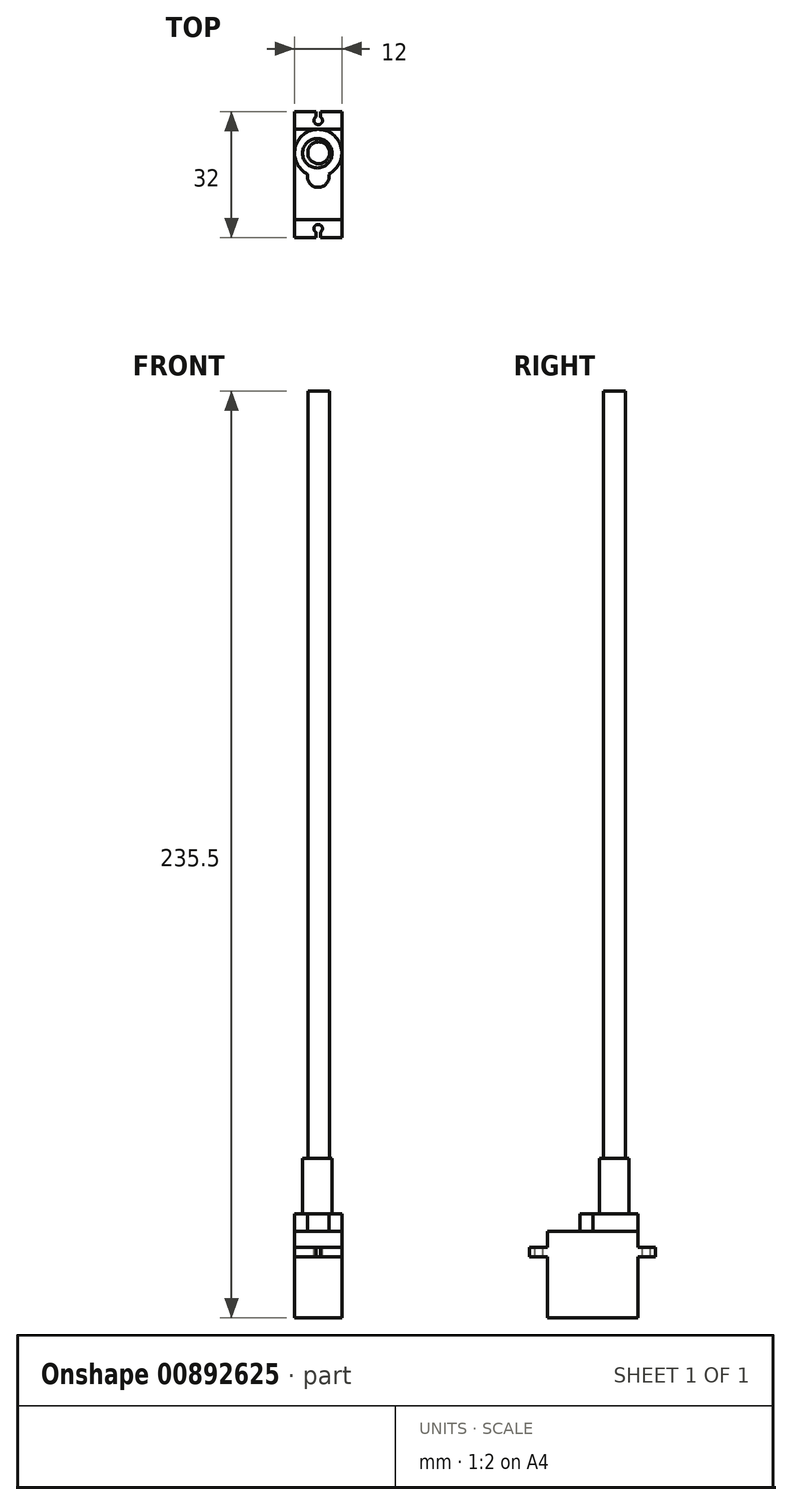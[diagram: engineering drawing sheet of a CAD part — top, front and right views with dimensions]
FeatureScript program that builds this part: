
annotation { "Feature Type Name" : "Feature", "Feature Type Description" : "" }
export const myFeature = defineFeature(function(context is Context, id is Id, definition is map)
    precondition{}
    {
        {
            var Q0;
            Q0=qCreatedBy(makeId("Top.planeOp"),FACE);
            var sketch = newSketch(context, id + "F0", { "sketchPlane" : qUnion([Q0])});
            skLineSegment(sketch, "E0.bottom", {"start": v(0, 0) * mm, "end": v(12, 0) * mm});
            skLineSegment(sketch, "E0.top", {"start": v(0, 23) * mm, "end": v(12, 23) * mm});
            skLineSegment(sketch, "E0.left", {"start": v(0, 0) * mm, "end": v(0, 23) * mm});
            skLineSegment(sketch, "E0.right", {"start": v(12, 0) * mm, "end": v(12, 23) * mm});
            skSolve(sketch);
        }
        {
            var Q0;
            Q0=qSketchRegion(id+"F0",true);
            extrude(context, id + "F1", {"entities" : qUnion([Q0]), "depth" : 22 * mm, "offsetDistance" : 25 * mm});
        }
        {
            var Q0;
            Q0=qCreatedBy(makeId("Top.planeOp"),FACE);
            cPlane(context, id + "F2", {"entities" : qUnion([Q0]), "cplaneType" : CPlaneType.OFFSET, "offset" : 15.5 * mm, "width" : 150 * mm, "height" : 150 * mm});
        }
        {
            var Q0;
            Q0=qCreatedBy(id+"F2.planeOp",FACE);
            var sketch = newSketch(context, id + "F3", { "sketchPlane" : qUnion([Q0])});
            skLineSegment(sketch, "E1.0", {"start": v(0, 23) * mm, "end": v(12, 23) * mm});
            skPoint(sketch, "E2.0", {"position": v(0, 11.5) * mm});
            skPoint(sketch, "E3.0", {"position": v(12, 11.5) * mm});
            skLineSegment(sketch, "E4", {"start": v(0, 11.5) * mm, "end": v(12, 11.5) * mm, "construction": true});
            skLineSegment(sketch, "E5", {"start": v(0, 23) * mm, "end": v(0, 27.5) * mm});
            skLineSegment(sketch, "E6", {"start": v(0, 27.5) * mm, "end": v(12, 27.5) * mm});
            skLineSegment(sketch, "E7", {"start": v(12, 27.5) * mm, "end": v(12, 23) * mm});
            skLineSegment(sketch, "E8.MirrorCS", {"start": v(0, 0) * mm, "end": v(12, 0) * mm});
            skLineSegment(sketch, "E9.MirrorCS", {"start": v(0, 0) * mm, "end": v(0, -4.5) * mm});
            skLineSegment(sketch, "E10.MirrorCS", {"start": v(0, -4.5) * mm, "end": v(12, -4.5) * mm});
            skLineSegment(sketch, "E11.MirrorCS", {"start": v(12, -4.5) * mm, "end": v(12, 0) * mm});
            skSolve(sketch);
        }
        {
            var Q0;
            Q0=qSketchRegion(id+"F3",true);
            extrude(context, id + "F4", {"entities" : qUnion([Q0]), "operationType" : NewBodyOperationType.ADD, "depth" : 2.5 * mm, "offsetDistance" : 25 * mm});
        }
        {
            var Q0;
            Q0=makeQuery(id+"F4.opExtrude","CAP_FACE",FACE,{"disambiguationData":[OSD([sQuery(id+"F3.wireOp",EDGE,"E1.0"),sQuery(id+"F3.wireOp",EDGE,"E5"),sQuery(id+"F3.wireOp",EDGE,"E6"),sQuery(id+"F3.wireOp",EDGE,"E7")])],"isStart":false});
            var sketch = newSketch(context, id + "F5", { "sketchPlane" : qUnion([Q0])});
            skCircle(sketch, "E12", {"center": v(6, 25.25) * mm, "radius": 1.07 * mm});
            skPoint(sketch, "E12.centerSnap0", {"position": v(12, 25.25) * mm});
            skPoint(sketch, "E12.centerSnap1", {"position": v(6, 27.5) * mm});
            skLineSegment(sketch, "E13", {"start": v(6, 27.5) * mm, "end": v(6, 25.25) * mm, "construction": true});
            skLineSegment(sketch, "E14", {"start": v(5.42, 27.5) * mm, "end": v(5.42, 26.16) * mm});
            skLineSegment(sketch, "E15", {"start": v(6.58, 27.5) * mm, "end": v(6.58, 26.16) * mm});
            skLineSegment(sketch, "E16", {"start": v(5.42, 27.5) * mm, "end": v(6, 27.5) * mm, "construction": true});
            skLineSegment(sketch, "E17", {"start": v(6, 27.5) * mm, "end": v(6.58, 27.5) * mm, "construction": true});
            skLineSegment(sketch, "E18.0.0", {"start": v(12, 23) * mm, "end": v(0, 23) * mm, "construction": true});
            skLineSegment(sketch, "E18.0.1", {"start": v(0, 23) * mm, "end": v(0, 0) * mm, "construction": true});
            skLineSegment(sketch, "E18.0.2", {"start": v(0, 0) * mm, "end": v(12, 0) * mm, "construction": true});
            skLineSegment(sketch, "E18.0.3", {"start": v(12, 0) * mm, "end": v(12, 23) * mm, "construction": true});
            skLineSegment(sketch, "E19", {"start": v(0, 11.5) * mm, "end": v(12, 11.5) * mm, "construction": true});
            skLineSegment(sketch, "E20.MirrorCS", {"start": v(6.58, -4.5) * mm, "end": v(6.58, -3.16) * mm});
            skCircle(sketch, "E21.MirrorC", {"center": v(6, -2.25) * mm, "radius": 1.07 * mm});
            skLineSegment(sketch, "E22.MirrorCS", {"start": v(6, -4.5) * mm, "end": v(6, -2.25) * mm, "construction": true});
            skPoint(sketch, "E23.MirrorP", {"position": v(6, -4.5) * mm});
            skLineSegment(sketch, "E24.MirrorCS", {"start": v(5.42, -4.5) * mm, "end": v(5.42, -3.16) * mm});
            skLineSegment(sketch, "E25", {"start": v(5.42, 27.5) * mm, "end": v(6.58, 27.5) * mm});
            skLineSegment(sketch, "E26.MirrorCS", {"start": v(5.42, -4.5) * mm, "end": v(6.58, -4.5) * mm});
            skLineSegment(sketch, "E27.MirrorCS", {"start": v(5.42, -4.5) * mm, "end": v(6, -4.5) * mm, "construction": true});
            skLineSegment(sketch, "E28.MirrorCS", {"start": v(6, -4.5) * mm, "end": v(6.58, -4.5) * mm, "construction": true});
            skSolve(sketch);
        }
        {
            var Q0;
            Q0=qSketchRegion(id+"F5",true);
            extrude(context, id + "F6", {"entities" : qUnion([Q0]), "operationType" : NewBodyOperationType.REMOVE, "endBound" : BoundingType.THROUGH_ALL, "oppositeDirection" : true, "depth" : 25 * mm, "offsetDistance" : 25 * mm});
        }
        {
            var Q0;
            Q0=makeQuery(id+"F1.opExtrude","CAP_FACE",FACE,{"disambiguationData":[OSD([sQuery(id+"F0.wireOp",EDGE,"E0.bottom"),sQuery(id+"F0.wireOp",EDGE,"E0.top"),sQuery(id+"F0.wireOp",EDGE,"E0.left"),sQuery(id+"F0.wireOp",EDGE,"E0.right")])],"isStart":false});
            var sketch = newSketch(context, id + "F7", { "sketchPlane" : qUnion([Q0])});
            skCircle(sketch, "E29", {"center": v(6, 17) * mm, "radius": 6 * mm});
            skPoint(sketch, "E29.centerSnap0", {"position": v(6, 23) * mm});
            skArc(sketch, "E30", {"start": v(3.32, 11.63) * mm, "mid": v(6, 8.25) * mm, "end": v(8.68, 11.63) * mm});
            skSolve(sketch);
        }
        {
            var Q0;
            Q0=qSketchRegion(id+"F7",true);
            extrude(context, id + "F8", {"entities" : qUnion([Q0]), "operationType" : NewBodyOperationType.ADD, "depth" : 4.5 * mm, "offsetDistance" : 25 * mm});
        }
        {
            var Q0;
            Q0=makeQuery(id+"F8.opExtrude","CAP_FACE",FACE,{"disambiguationData":[OSD([sQuery(id+"F7.wireOp",EDGE,"E29"),sQuery(id+"F7.wireOp",EDGE,"E30")])],"isStart":false});
            var sketch = newSketch(context, id + "F9", { "sketchPlane" : qUnion([Q0])});
            skCircle(sketch, "E31", {"center": v(6, 17) * mm, "radius": 2.43 * mm});
            skSolve(sketch);
        }
        {
            var Q0;
            Q0=qSketchRegion(id+"F9",true);
            extrude(context, id + "F10", {"entities" : qUnion([Q0]), "operationType" : NewBodyOperationType.ADD, "depth" : 3 * mm, "offsetDistance" : 25 * mm});
        }
        {
            var Q0;
            Q0=qCreatedBy(id+"F2.planeOp",FACE);
            var sketch = newSketch(context, id + "F11", { "sketchPlane" : qUnion([Q0])});
            skCircle(sketch, "E32", {"center": v(5.77, 16.94) * mm, "radius": 3.74 * mm});
            skSolve(sketch);
        }
        {
            var Q0;
            Q0=qSketchRegion(id+"F11",true);
            extrude(context, id + "F12", {"entities" : qUnion([Q0]), "operationType" : NewBodyOperationType.ADD, "depth" : 25 * mm, "offsetDistance" : 25 * mm});
        }
        {
            var Q0;
            Q0=qCreatedBy(id+"F2.planeOp",FACE);
            var sketch = newSketch(context, id + "F13", { "sketchPlane" : qUnion([Q0])});
            skCircle(sketch, "E33", {"center": v(6.12, 17.04) * mm, "radius": 2.77 * mm});
            skSolve(sketch);
        }
        {
            var Q0;
            Q0=qSketchRegion(id+"F13",true);
            extrude(context, id + "F14", {"entities" : qUnion([Q0]), "operationType" : NewBodyOperationType.ADD, "depth" : 220 * mm, "offsetDistance" : 25 * mm});
        }
    });
